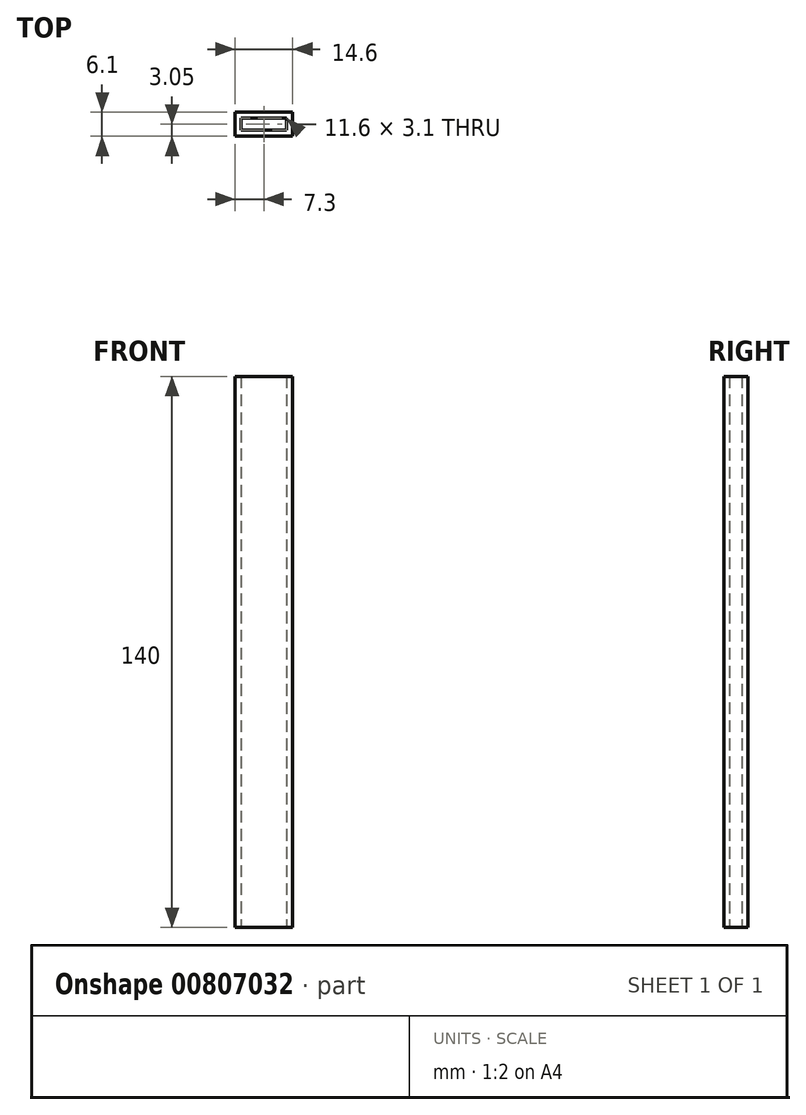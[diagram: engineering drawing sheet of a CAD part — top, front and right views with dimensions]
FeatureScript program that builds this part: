
annotation { "Feature Type Name" : "Feature", "Feature Type Description" : "" }
export const myFeature = defineFeature(function(context is Context, id is Id, definition is map)
    precondition{}
    {
        {
            var Q0;
            Q0=qCreatedBy(makeId("Front.planeOp"),FACE);
            var sketch = newSketch(context, id + "F0", { "sketchPlane" : qUnion([Q0])});
            skLineSegment(sketch, "E0.bottom", {"start": v(7.3, 70) * mm, "end": v(-7.3, 70) * mm});
            skLineSegment(sketch, "E0.top", {"start": v(7.3, -70) * mm, "end": v(-7.3, -70) * mm});
            skLineSegment(sketch, "E0.left", {"start": v(7.3, 70) * mm, "end": v(7.3, -70) * mm});
            skLineSegment(sketch, "E0.right", {"start": v(-7.3, 70) * mm, "end": v(-7.3, -70) * mm});
            skPoint(sketch, "E0.middle", {"position": v(0, 0) * mm});
            skSolve(sketch);
        }
        {
            var Q0;
            Q0=makeQuery(id+"F0.imprint","IMPRINT",FACE,{"disambiguationData":[TD([[makeQuery(id+"F0.imprint","IMPRINT",EDGE,{"derivedFrom":sQuery(id+"F0.wireOp",EDGE,"E0.bottom")}),1.0]])]});
            extrude(context, id + "F1", {"entities" : qUnion([Q0]), "depth" : 6.1 * mm, "offsetDistance" : 25 * mm});
        }
        {
            var Q0;
            Q0=makeQuery(id+"F1.opExtrude","SWEPT_FACE",FACE,{"disambiguationData":[OSD([sQuery(id+"F0.wireOp",EDGE,"E0.top")])]});
            var Q1;
            Q1=makeQuery(id+"F1.opExtrude","SWEPT_FACE",FACE,{"disambiguationData":[OSD([sQuery(id+"F0.wireOp",EDGE,"E0.bottom")])]});
            shell(context, id + "F2", {"entities" : qUnion([Q0, Q1]), "thickness" : 1.5 * mm});
        }
    });
